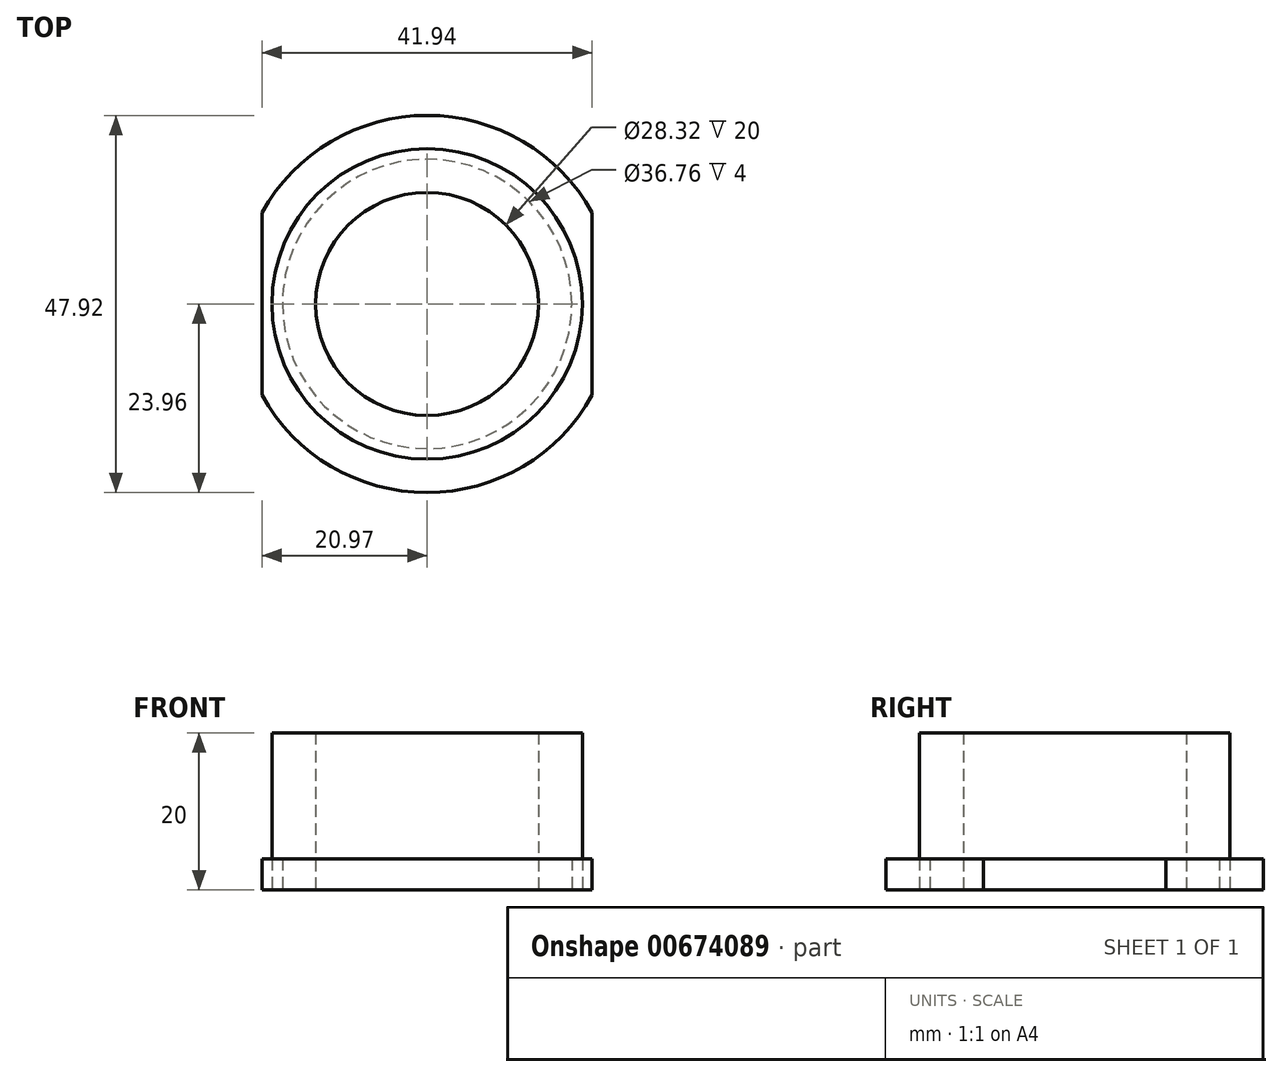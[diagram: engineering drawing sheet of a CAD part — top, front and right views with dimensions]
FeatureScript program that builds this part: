
annotation { "Feature Type Name" : "Feature", "Feature Type Description" : "" }
export const myFeature = defineFeature(function(context is Context, id is Id, definition is map)
    precondition{}
    {
        {
            var Q0;
            Q0=qCreatedBy(makeId("Top.planeOp"),FACE);
            var sketch = newSketch(context, id + "F0", { "sketchPlane" : qUnion([Q0])});
            skCircle(sketch, "E0", {"center": v(0, 0) * mm, "radius": 23.96 * mm});
            skLineSegment(sketch, "E1.bottom", {"start": v(20.97, 30.02) * mm, "end": v(-20.97, 30.02) * mm});
            skLineSegment(sketch, "E1.top", {"start": v(20.97, -30.02) * mm, "end": v(-20.97, -30.02) * mm});
            skLineSegment(sketch, "E1.left", {"start": v(20.97, 30.02) * mm, "end": v(20.97, -30.02) * mm});
            skLineSegment(sketch, "E1.right", {"start": v(-20.97, 30.02) * mm, "end": v(-20.97, -30.02) * mm});
            skCircle(sketch, "E2", {"center": v(0, 0) * mm, "radius": 14.16 * mm});
            skCircle(sketch, "E3", {"center": v(0, 0) * mm, "radius": 18.38 * mm});
            skCircle(sketch, "E4", {"center": v(0, 0) * mm, "radius": 19.71 * mm});
            skSolve(sketch);
        }
        {
            var Q0;
            Q0=makeQuery(id+"F0.imprint","IMPRINT",FACE,{"disambiguationData":[TD([[makeQuery(id+"F0.imprint","IMPRINT",EDGE,{"derivedFrom":sQuery(id+"F0.wireOp",EDGE,"E4")}),-1.0]])]});
            var Q1;
            Q1=makeQuery(id+"F0.imprint","IMPRINT",FACE,{"disambiguationData":[TD([[makeQuery(id+"F0.imprint","IMPRINT",EDGE,{"derivedFrom":sQuery(id+"F0.wireOp",EDGE,"E3")}),-1.0]])]});
            extrude(context, id + "F1", {"entities" : qUnion([Q0, Q1]), "depth" : 4 * mm, "offsetDistance" : 25 * mm});
        }
        {
            var Q0;
            Q0=makeQuery(id+"F0.imprint","IMPRINT",FACE,{"disambiguationData":[TD([[makeQuery(id+"F0.imprint","IMPRINT",EDGE,{"derivedFrom":sQuery(id+"F0.wireOp",EDGE,"E3")}),-1.0]])]});
            var Q1;
            Q1=makeQuery(id+"F0.imprint","IMPRINT",FACE,{"disambiguationData":[TD([[makeQuery(id+"F0.imprint","IMPRINT",EDGE,{"derivedFrom":sQuery(id+"F0.wireOp",EDGE,"E2")}),-1.0]])]});
            extrude(context, id + "F2", {"entities" : qUnion([Q0, Q1]), "depth" : 20 * mm, "offsetDistance" : 25 * mm});
        }
    });
